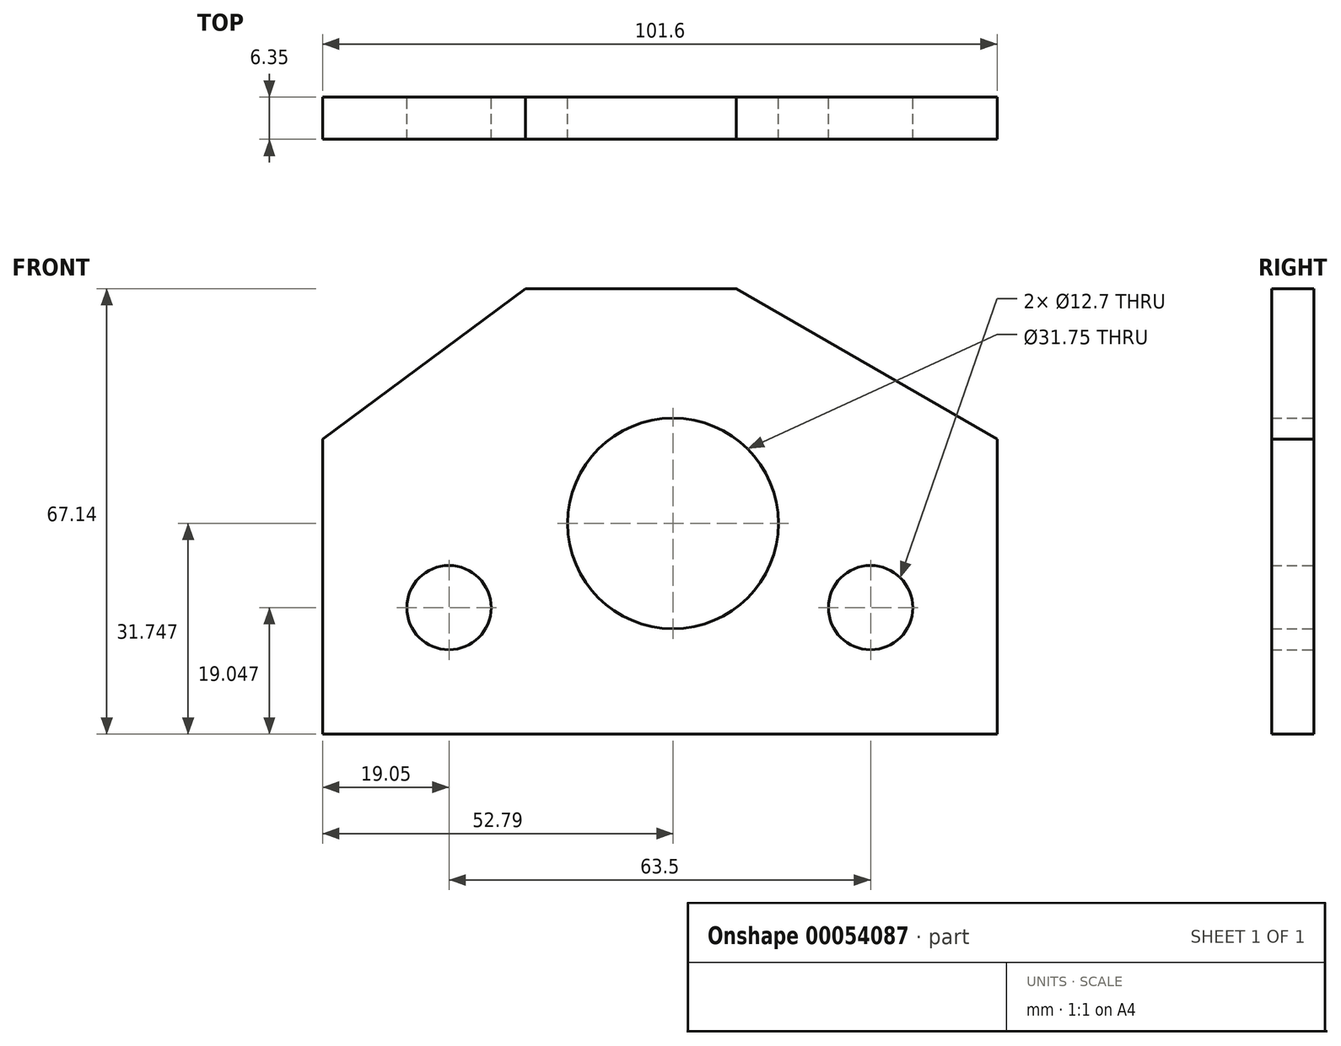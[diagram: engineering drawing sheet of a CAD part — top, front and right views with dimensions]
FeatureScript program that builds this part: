
annotation { "Feature Type Name" : "Feature", "Feature Type Description" : "" }
export const myFeature = defineFeature(function(context is Context, id is Id, definition is map)
    precondition{}
    {
        {
            var Q0;
            Q0=qCreatedBy(makeId("Front.planeOp"),FACE);
            var sketch = newSketch(context, id + "F0", { "sketchPlane" : qUnion([Q0])});
            skLineSegment(sketch, "E0", {"start": v(-52.8, -33.57) * mm, "end": v(48.8, -33.57) * mm});
            skLineSegment(sketch, "E1", {"start": v(48.8, -33.57) * mm, "end": v(48.8, 10.88) * mm});
            skLineSegment(sketch, "E2", {"start": v(-52.8, -33.57) * mm, "end": v(-52.8, 10.88) * mm});
            skLineSegment(sketch, "E3", {"start": v(-22.2, 33.57) * mm, "end": v(9.55, 33.57) * mm});
            skLineSegment(sketch, "E4", {"start": v(-52.8, 10.88) * mm, "end": v(-22.2, 33.57) * mm});
            skLineSegment(sketch, "E5", {"start": v(9.55, 33.57) * mm, "end": v(48.8, 10.88) * mm});
            skCircle(sketch, "E6", {"center": v(0, -1.82) * mm, "radius": 15.88 * mm});
            skCircle(sketch, "E7", {"center": v(-33.74, -14.52) * mm, "radius": 6.35 * mm});
            skCircle(sketch, "E8", {"center": v(29.76, -14.52) * mm, "radius": 6.35 * mm});
            skSolve(sketch);
        }
        {
            var Q0;
            Q0 = qSketchRegion(id + "F0", true);
            extrude(context, id + "F1", {"entities" : qUnion([Q0]), "depth" : 6.35 * mm});
        }
    });
